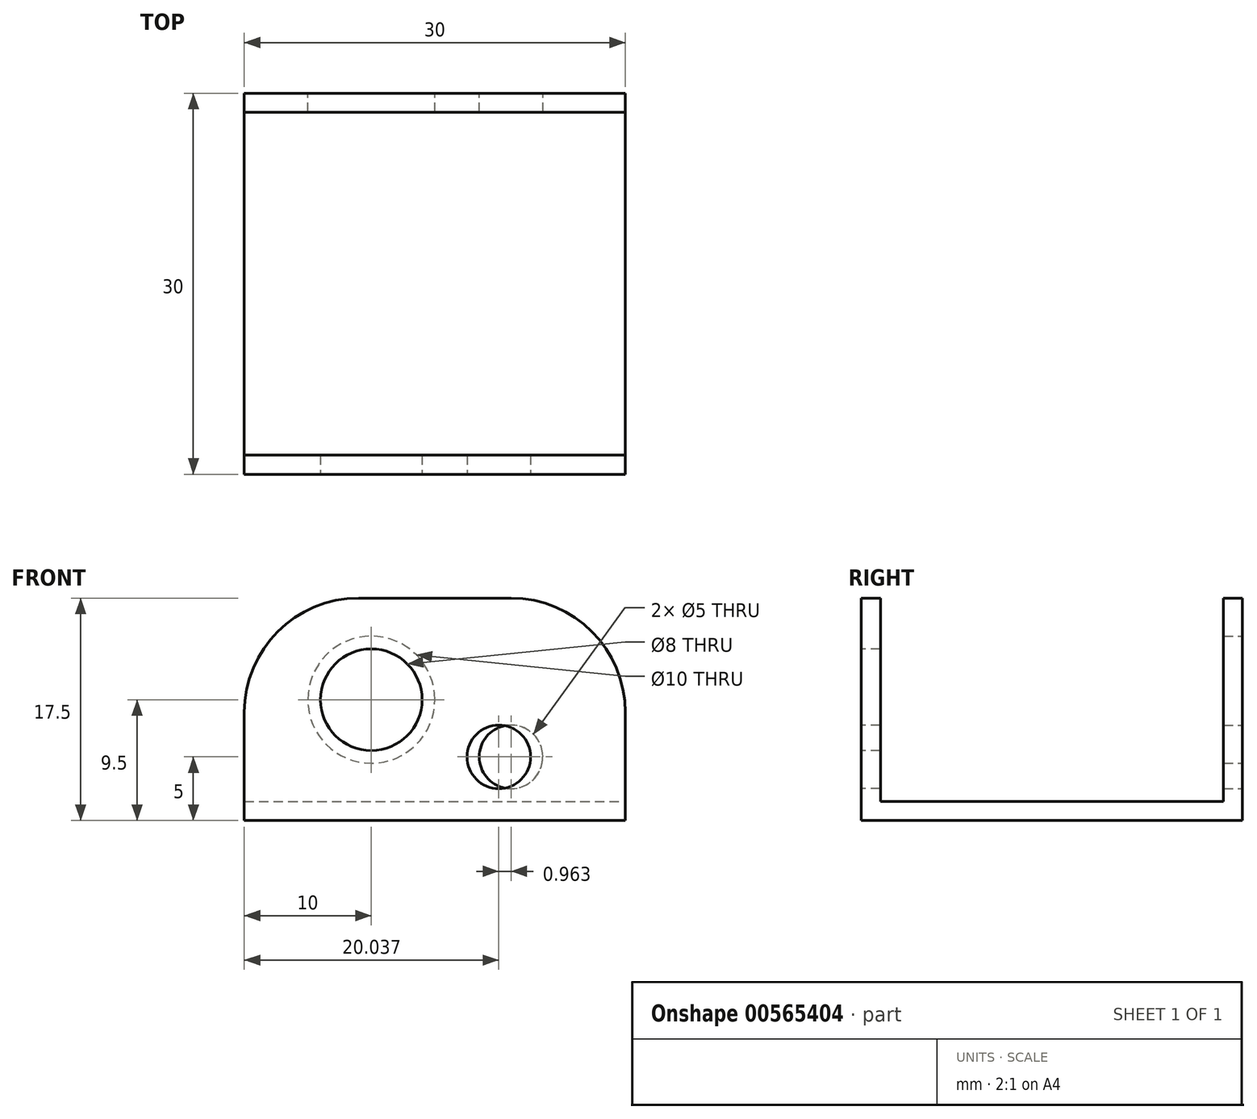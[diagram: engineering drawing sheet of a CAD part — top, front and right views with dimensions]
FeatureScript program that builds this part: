
annotation { "Feature Type Name" : "Feature", "Feature Type Description" : "" }
export const myFeature = defineFeature(function(context is Context, id is Id, definition is map)
    precondition{}
    {
        {
            var Q0;
            Q0=qCreatedBy(makeId("Top.planeOp"),FACE);
            var sketch = newSketch(context, id + "F0", { "sketchPlane" : qUnion([Q0])});
            skLineSegment(sketch, "E0.bottom", {"start": v(-15, 15) * mm, "end": v(15, 15) * mm});
            skLineSegment(sketch, "E0.top", {"start": v(-15, -15) * mm, "end": v(15, -15) * mm});
            skLineSegment(sketch, "E0.left", {"start": v(-15, 15) * mm, "end": v(-15, -15) * mm});
            skLineSegment(sketch, "E0.right", {"start": v(15, 15) * mm, "end": v(15, -15) * mm});
            skSolve(sketch);
        }
        {
            var Q0;
            Q0=makeQuery(id+"F0.imprint","IMPRINT",FACE,{"disambiguationData":[TD([[makeQuery(id+"F0.imprint","IMPRINT",EDGE,{"derivedFrom":sQuery(id+"F0.wireOp",EDGE,"E0.bottom")}),-1.0]])]});
            extrude(context, id + "F1", {"entities" : qUnion([Q0]), "depth" : 1.5 * mm, "offsetDistance" : 25 * mm});
        }
        {
            var Q0;
            Q0=makeQuery(id+"F1.opExtrude","CAP_FACE",FACE,{"disambiguationData":[OSD([sQuery(id+"F0.wireOp",EDGE,"E0.bottom"),sQuery(id+"F0.wireOp",EDGE,"E0.top"),sQuery(id+"F0.wireOp",EDGE,"E0.left"),sQuery(id+"F0.wireOp",EDGE,"E0.right")])],"isStart":false});
            var sketch = newSketch(context, id + "F2", { "sketchPlane" : qUnion([Q0])});
            skLineSegment(sketch, "E1.bottom", {"start": v(-15, 15) * mm, "end": v(15, 15) * mm});
            skLineSegment(sketch, "E1.top", {"start": v(-15, 13.5) * mm, "end": v(15, 13.5) * mm});
            skLineSegment(sketch, "E1.left", {"start": v(-15, 15) * mm, "end": v(-15, 13.5) * mm});
            skLineSegment(sketch, "E1.right", {"start": v(15, 15) * mm, "end": v(15, 13.5) * mm});
            skSolve(sketch);
        }
        {
            var Q0;
            Q0=makeQuery(id+"F2.imprint","IMPRINT",FACE,{"disambiguationData":[TD([[makeQuery(id+"F2.imprint","IMPRINT",EDGE,{"derivedFrom":sQuery(id+"F2.wireOp",EDGE,"E1.bottom")}),-1.0]])]});
            extrude(context, id + "F3", {"entities" : qUnion([Q0]), "operationType" : NewBodyOperationType.ADD, "depth" : 16 * mm, "offsetDistance" : 25 * mm});
        }
        {
            var Q0;
            Q0=makeQuery(id+"F1.opExtrude","CAP_FACE",FACE,{"disambiguationData":[OSD([sQuery(id+"F0.wireOp",EDGE,"E0.bottom"),sQuery(id+"F0.wireOp",EDGE,"E0.top"),sQuery(id+"F0.wireOp",EDGE,"E0.left"),sQuery(id+"F0.wireOp",EDGE,"E0.right")])],"isStart":false});
            var sketch = newSketch(context, id + "F4", { "sketchPlane" : qUnion([Q0])});
            skLineSegment(sketch, "E2.bottom", {"start": v(-15, -15) * mm, "end": v(15, -15) * mm});
            skLineSegment(sketch, "E2.top", {"start": v(-15, -13.5) * mm, "end": v(15, -13.5) * mm});
            skLineSegment(sketch, "E2.left", {"start": v(-15, -15) * mm, "end": v(-15, -13.5) * mm});
            skLineSegment(sketch, "E2.right", {"start": v(15, -15) * mm, "end": v(15, -13.5) * mm});
            skSolve(sketch);
        }
        {
            var Q0;
            Q0=makeQuery(id+"F4.imprint","IMPRINT",FACE,{"disambiguationData":[TD([[makeQuery(id+"F4.imprint","IMPRINT",EDGE,{"derivedFrom":sQuery(id+"F4.wireOp",EDGE,"E2.bottom")}),1.0]])]});
            extrude(context, id + "F5", {"entities" : qUnion([Q0]), "operationType" : NewBodyOperationType.ADD, "depth" : 16 * mm, "offsetDistance" : 25 * mm});
        }
        {
            var Q0;
            Q0=makeQuery(id+"F5.boolean.opBoolean","MERGE",FACE,{"derivedFrom":[makeQuery(id+"F1.opExtrude","SWEPT_FACE",FACE,{"disambiguationData":[OSD([sQuery(id+"F0.wireOp",EDGE,"E0.top")])]}),makeQuery(id+"F5.opExtrude","SWEPT_FACE",FACE,{"disambiguationData":[OSD([sQuery(id+"F4.wireOp",EDGE,"E2.bottom")])]})]});
            var sketch = newSketch(context, id + "F6", { "sketchPlane" : qUnion([Q0])});
            skCircle(sketch, "E3", {"center": v(-5, 9.5) * mm, "radius": 4 * mm});
            skCircle(sketch, "E4", {"center": v(5.04, 5) * mm, "radius": 2.5 * mm});
            skSolve(sketch);
        }
        {
            var Q0;
            Q0=makeQuery(id+"F6.imprint","IMPRINT",FACE,{"disambiguationData":[TD([[makeQuery(id+"F6.imprint","IMPRINT",EDGE,{"derivedFrom":sQuery(id+"F6.wireOp",EDGE,"E3")}),1.0]])]});
            var Q1;
            Q1=makeQuery(id+"F6.imprint","IMPRINT",FACE,{"disambiguationData":[TD([[makeQuery(id+"F6.imprint","IMPRINT",EDGE,{"derivedFrom":sQuery(id+"F6.wireOp",EDGE,"E4")}),1.0]])]});
            extrude(context, id + "F7", {"entities" : qUnion([Q0, Q1]), "operationType" : NewBodyOperationType.REMOVE, "oppositeDirection" : true, "depth" : 25 * mm, "offsetDistance" : 25 * mm});
        }
        {
            var Q0;
            Q0=makeQuery(id+"F3.boolean.opBoolean","MERGE",FACE,{"derivedFrom":[makeQuery(id+"F1.opExtrude","SWEPT_FACE",FACE,{"disambiguationData":[OSD([sQuery(id+"F0.wireOp",EDGE,"E0.bottom")])]}),makeQuery(id+"F3.opExtrude","SWEPT_FACE",FACE,{"disambiguationData":[OSD([sQuery(id+"F2.wireOp",EDGE,"E1.bottom")])]})]});
            var sketch = newSketch(context, id + "F8", { "sketchPlane" : qUnion([Q0])});
            skCircle(sketch, "E5", {"center": v(-6, 5) * mm, "radius": 2.5 * mm});
            skCircle(sketch, "E6", {"center": v(5, 9.5) * mm, "radius": 5 * mm});
            skSolve(sketch);
        }
        {
            var Q0;
            Q0=makeQuery(id+"F8.imprint","IMPRINT",FACE,{"disambiguationData":[TD([[makeQuery(id+"F8.imprint","IMPRINT",EDGE,{"derivedFrom":sQuery(id+"F8.wireOp",EDGE,"E6")}),1.0]])]});
            var Q1;
            Q1=makeQuery(id+"F8.imprint","IMPRINT",FACE,{"disambiguationData":[TD([[makeQuery(id+"F8.imprint","IMPRINT",EDGE,{"derivedFrom":sQuery(id+"F8.wireOp",EDGE,"E5")}),1.0]])]});
            extrude(context, id + "F9", {"entities" : qUnion([Q0, Q1]), "operationType" : NewBodyOperationType.REMOVE, "oppositeDirection" : true, "depth" : 25 * mm, "offsetDistance" : 25 * mm});
        }
        {
            var Q0;
            Q0=makeQuery(id+"F3.opExtrude","CAP_EDGE",EDGE,{"disambiguationData":[OSD([sQuery(id+"F2.wireOp",EDGE,"E1.right")])],"isStart":false});
            var Q1;
            Q1=makeQuery(id+"F5.opExtrude","CAP_EDGE",EDGE,{"disambiguationData":[OSD([sQuery(id+"F4.wireOp",EDGE,"E2.right")])],"isStart":false});
            var Q2;
            Q2=makeQuery(id+"F5.opExtrude","CAP_EDGE",EDGE,{"disambiguationData":[OSD([sQuery(id+"F4.wireOp",EDGE,"E2.left")])],"isStart":false});
            var Q3;
            Q3=makeQuery(id+"F3.opExtrude","CAP_EDGE",EDGE,{"disambiguationData":[OSD([sQuery(id+"F2.wireOp",EDGE,"E1.left")])],"isStart":false});
            fillet(context, id + "F10", {"entities" : qUnion([Q0, Q1, Q2, Q3]), "radius" : 9 * mm, "tangentPropagation" : true, "allowEdgeOverflow" : false});
        }
    });
